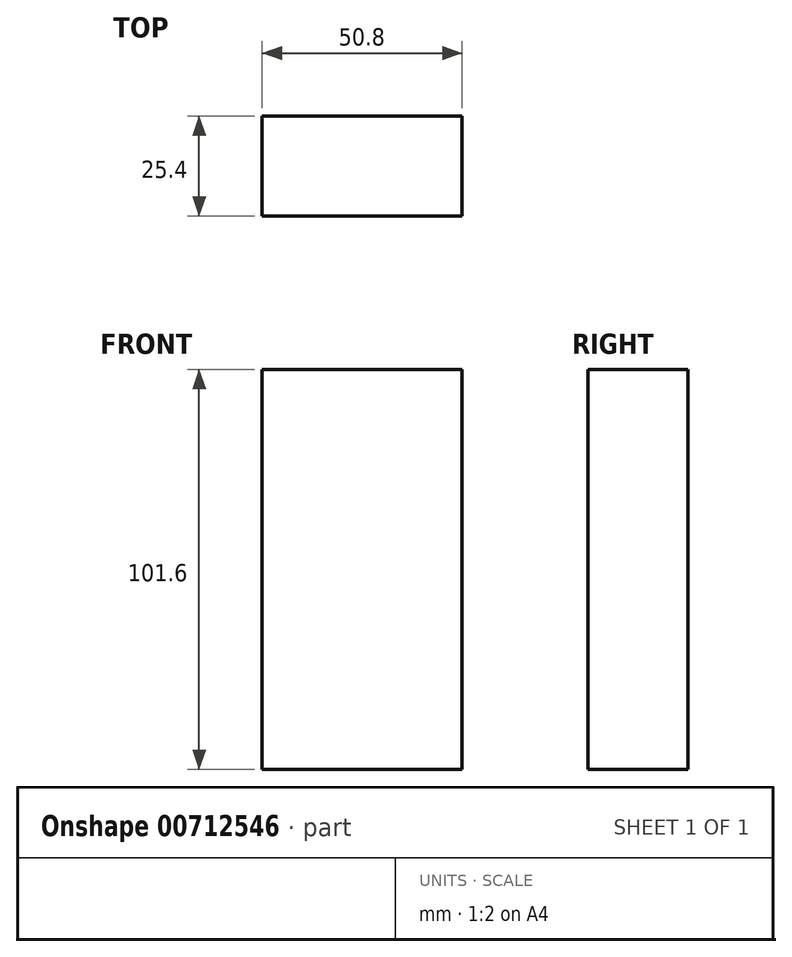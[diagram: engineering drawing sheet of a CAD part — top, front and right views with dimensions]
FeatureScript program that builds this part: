
annotation { "Feature Type Name" : "Feature", "Feature Type Description" : "" }
export const myFeature = defineFeature(function(context is Context, id is Id, definition is map)
    precondition{}
    {
        {
            var Q0;
            Q0=qCreatedBy(makeId("Top.planeOp"),FACE);
            var sketch = newSketch(context, id + "F0", { "sketchPlane" : qUnion([Q0])});
            skLineSegment(sketch, "E0.bottom", {"start": v(25.4, -12.7) * mm, "end": v(-25.4, -12.7) * mm});
            skLineSegment(sketch, "E0.top", {"start": v(25.4, 12.7) * mm, "end": v(-25.4, 12.7) * mm});
            skLineSegment(sketch, "E0.left", {"start": v(25.4, -12.7) * mm, "end": v(25.4, 12.7) * mm});
            skLineSegment(sketch, "E0.right", {"start": v(-25.4, -12.7) * mm, "end": v(-25.4, 12.7) * mm});
            skPoint(sketch, "E0.middle", {"position": v(0, 0) * mm});
            skSolve(sketch);
        }
        {
            var Q0;
            Q0 = qSketchRegion(id + "F0", true);
            extrude(context, id + "F1", {"entities" : qUnion([Q0]), "depth" : 101.6 * mm, "offsetDistance" : 25.4 * mm});
        }
    });
